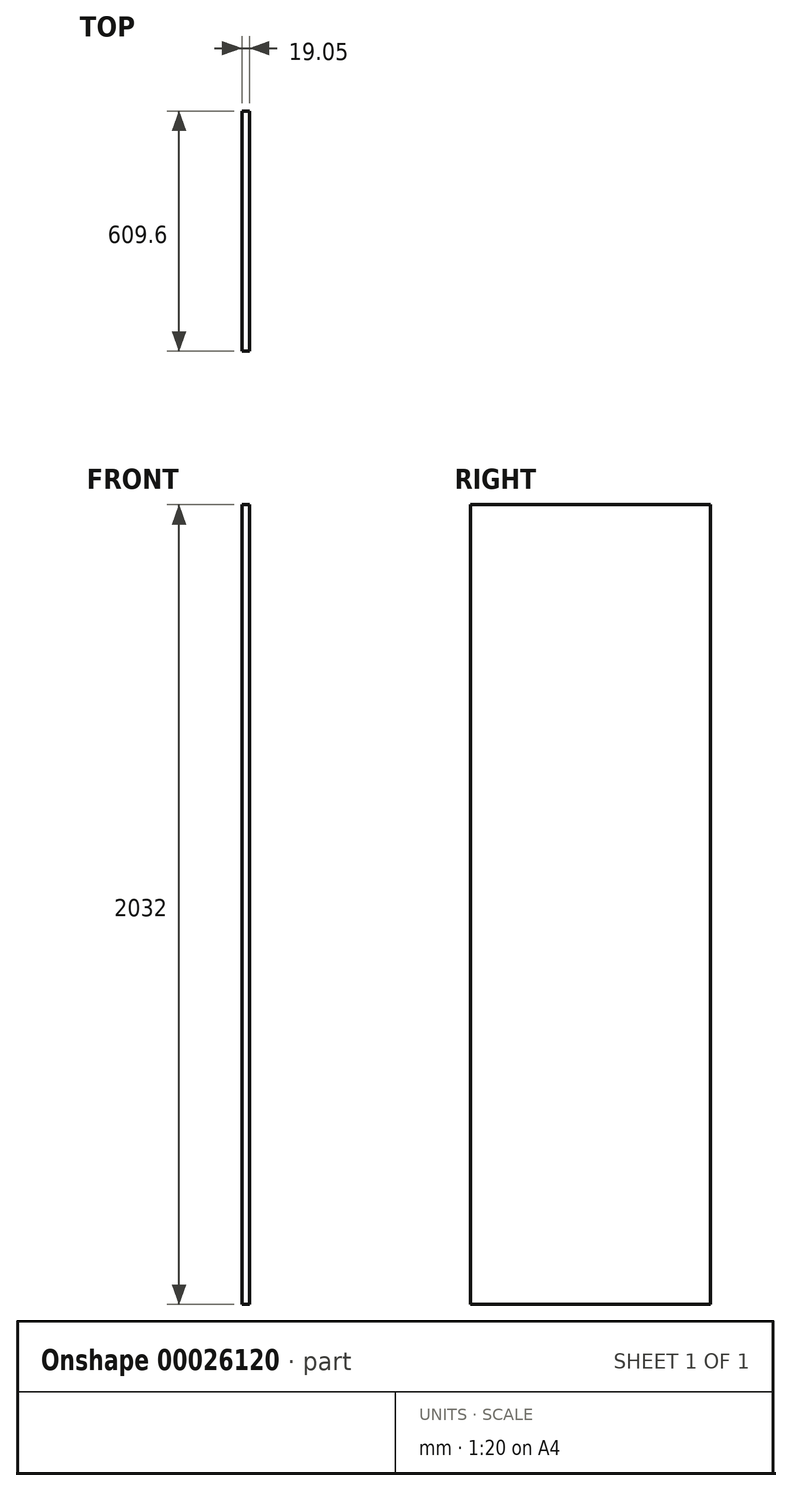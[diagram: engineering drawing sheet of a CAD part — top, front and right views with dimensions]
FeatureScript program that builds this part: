
annotation { "Feature Type Name" : "Feature", "Feature Type Description" : "" }
export const myFeature = defineFeature(function(context is Context, id is Id, definition is map)
    precondition{}
    {
        {
            var Q0;
            Q0=qCreatedBy(makeId("Front.planeOp"),FACE);
            var sketch = newSketch(context, id + "F0", { "sketchPlane" : qUnion([Q0])});
            skLineSegment(sketch, "E0.bottom", {"start": v(0, 0) * mm, "end": v(19.05, 0) * mm});
            skLineSegment(sketch, "E0.top", {"start": v(0, 2032) * mm, "end": v(19.05, 2032) * mm});
            skLineSegment(sketch, "E0.left", {"start": v(0, 0) * mm, "end": v(0, 2032) * mm});
            skLineSegment(sketch, "E0.right", {"start": v(19.05, 0) * mm, "end": v(19.05, 2032) * mm});
            skSolve(sketch);
        }
        {
            var Q0;
            Q0 = qSketchRegion(id + "F0", true);
            extrude(context, id + "F1", {"entities" : qUnion([Q0]), "oppositeDirection" : true, "depth" : 609.6 * mm});
        }
    });
